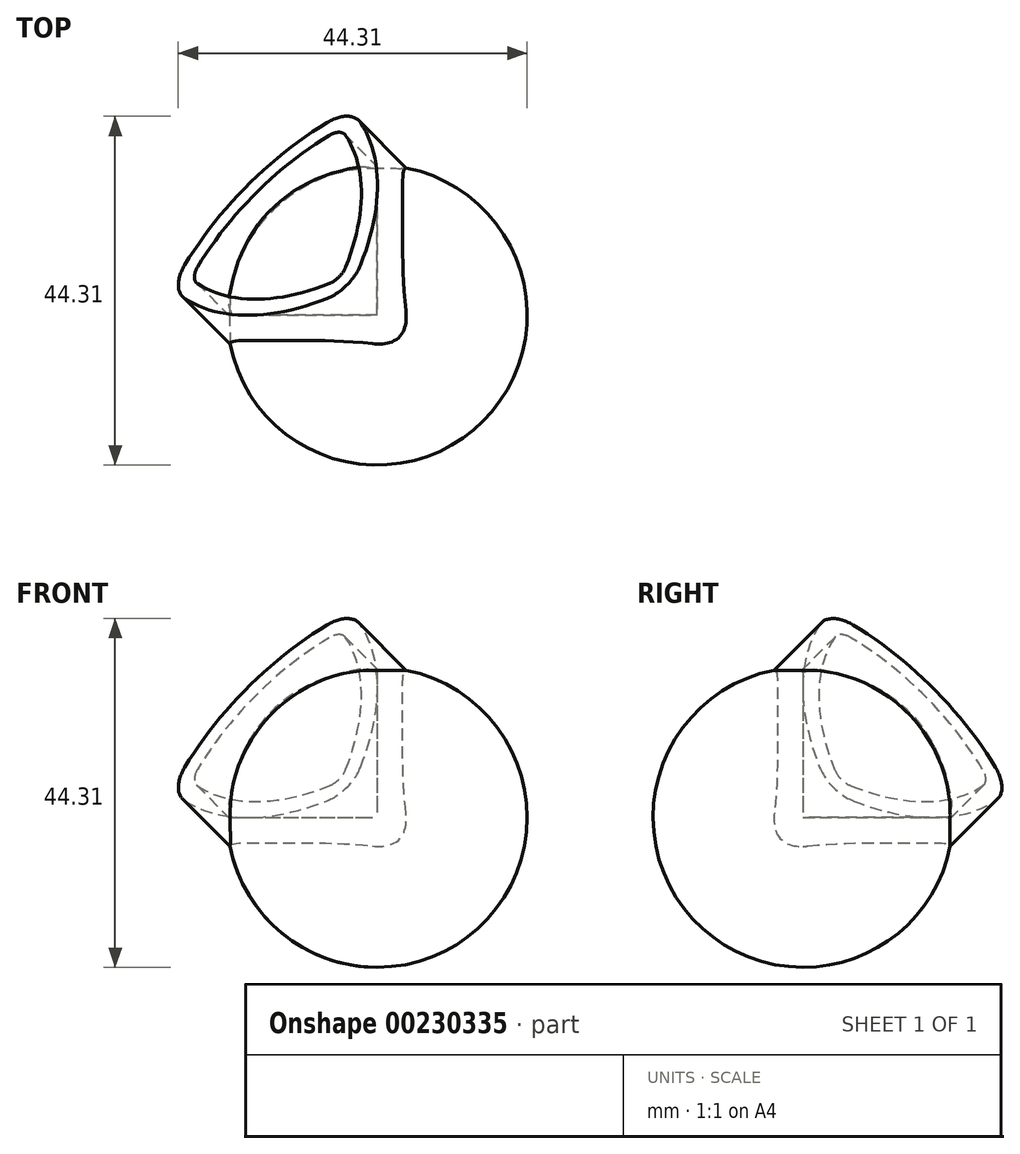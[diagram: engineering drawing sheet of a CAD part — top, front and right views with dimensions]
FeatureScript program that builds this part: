
annotation { "Feature Type Name" : "Feature", "Feature Type Description" : "" }
export const myFeature = defineFeature(function(context is Context, id is Id, definition is map)
    precondition{}
    {
        {
            var Q0;
            Q0=qCreatedBy(makeId("Front.planeOp"),FACE);
            var sketch = newSketch(context, id + "F0", { "sketchPlane" : qUnion([Q0])});
            skLineSegment(sketch, "E0", {"start": v(0, 19.05) * mm, "end": v(0, -19.05) * mm});
            skArc(sketch, "E1", {"start": v(0, 19.05) * mm, "mid": v(-19.05, 0) * mm, "end": v(0, -19.05) * mm});
            skSolve(sketch);
        }
        {
            var Q0;
            Q0=makeQuery(id+"F0.imprint","IMPRINT",FACE,{"disambiguationData":[TD([[makeQuery(id+"F0.imprint","IMPRINT",EDGE,{"derivedFrom":sQuery(id+"F0.wireOp",EDGE,"E0")}),-1.0]])]});
            var Q1;
            Q1=sQuery(id+"F0.wireOp",EDGE,"E0");
            revolve(context, id + "F1", {"entities" : qUnion([Q0]), "axis" : qUnion([Q1]), "revolveType" : RevolveType.FULL});
        }
        {
            var Q0;
            Q0=qCreatedBy(makeId("Front.planeOp"),FACE);
            var sketch = newSketch(context, id + "F2", { "sketchPlane" : qUnion([Q0])});
            skArc(sketch, "E2", {"start": v(0, 19.05) * mm, "mid": v(-13.47, 13.47) * mm, "end": v(-19.05, 0) * mm});
            skLineSegment(sketch, "E3", {"start": v(-19.05, 0) * mm, "end": v(0, 0) * mm});
            skLineSegment(sketch, "E4", {"start": v(0, 19.05) * mm, "end": v(0, 0) * mm});
            skSolve(sketch);
        }
        {
            var Q0;
            Q0=qSketchRegion(id+"F2",true);
            extrude(context, id + "F3", {"entities" : qUnion([Q0]), "operationType" : NewBodyOperationType.REMOVE, "oppositeDirection" : true, "depth" : 25 * mm});
        }
        {
            var Q0;
            Q0=makeQuery(id+"F3.boolean.opBoolean","COPY",VERTEX,{"derivedFrom":makeQuery(id+"F3.opExtrude","CAP_VERTEX",VERTEX,{"disambiguationData":[OSD([sQuery(id+"F2.wireOp",EDGE,"E2"),sQuery(id+"F2.wireOp",EDGE,"E4")])],"isStart":true})});
            var Q1;
            Q1=makeQuery(id+"F3.boolean.opBoolean","INTERSECT",VERTEX,{"derivedFrom":[makeQuery(id+"F1.opRevolve","SWEPT_FACE",FACE,{"disambiguationData":[OSD([sQuery(id+"F0.wireOp",EDGE,"E1")])]}),makeQuery(id+"F3.opExtrude","SWEPT_FACE",FACE,{"disambiguationData":[OSD([sQuery(id+"F2.wireOp",EDGE,"E3")])]}),makeQuery(id+"F3.opExtrude","SWEPT_FACE",FACE,{"disambiguationData":[OSD([sQuery(id+"F2.wireOp",EDGE,"E4")])]})]});
            var Q2;
            Q2=makeQuery(id+"F3.boolean.opBoolean","COPY",VERTEX,{"derivedFrom":makeQuery(id+"F3.opExtrude","CAP_VERTEX",VERTEX,{"disambiguationData":[OSD([sQuery(id+"F2.wireOp",EDGE,"E2"),sQuery(id+"F2.wireOp",EDGE,"E3")])],"isStart":true})});
            cPlane(context, id + "F4", {"entities" : qUnion([Q0, Q1, Q2]), "cplaneType" : CPlaneType.THREE_POINT, "offset" : 25 * mm, "width" : 150 * mm, "height" : 150 * mm});
        }
        {
            var Q0;
            Q0=qCreatedBy(id+"F4.planeOp",FACE);
            var sketch = newSketch(context, id + "F5", { "sketchPlane" : qUnion([Q0])});
            skArc(sketch, "E5", {"start": v(7.78, -13.47) * mm, "mid": v(10.97, 0) * mm, "end": v(7.78, 13.47) * mm});
            skArc(sketch, "E6", {"start": v(7.78, 13.47) * mm, "mid": v(-5.49, 9.5) * mm, "end": v(-15.55, 0) * mm});
            skArc(sketch, "E7", {"start": v(-15.55, 0) * mm, "mid": v(-5.49, -9.5) * mm, "end": v(7.78, -13.47) * mm});
            skArc(sketch, "E8.0", {"start": v(-18.5, 0) * mm, "mid": v(-6.74, -11.67) * mm, "end": v(9.25, -16.02) * mm});
            skArc(sketch, "E8.1", {"start": v(9.25, 16.02) * mm, "mid": v(-6.74, 11.67) * mm, "end": v(-18.5, 0) * mm});
            skArc(sketch, "E8.2", {"start": v(9.25, -16.02) * mm, "mid": v(13.47, 0) * mm, "end": v(9.25, 16.02) * mm});
            skSolve(sketch);
        }
        {
            var Q0;
            Q0=makeQuery(id+"F5.imprint","IMPRINT",FACE,{"disambiguationData":[TD([[makeQuery(id+"F5.imprint","IMPRINT",EDGE,{"derivedFrom":sQuery(id+"F5.wireOp",EDGE,"E5")}),-1.0]])]});
            var Q1;
            Q1=makeQuery(id+"F1.opRevolve","SWEPT_FACE",FACE,{"disambiguationData":[OSD([sQuery(id+"F0.wireOp",EDGE,"E1")])]});
            extrude(context, id + "F6", {"entities" : qUnion([Q0]), "operationType" : NewBodyOperationType.ADD, "endBoundEntityFace" : qUnion([Q1]), "depth" : 9.4 * mm, "hasSecondDirection" : true, "secondDirectionOppositeDirection" : true, "secondDirectionDepth" : 8 * mm});
        }
        {
            var Q0;
            Q0=qCreatedBy(makeId("Right.planeOp"),FACE);
            var Q1;
            Q1=qCreatedBy(makeId("Top.planeOp"),FACE);
            cPlane(context, id + "F7", {"entities" : qUnion([Q0, Q1]), "cplaneType" : CPlaneType.MID_PLANE, "offset" : 25 * mm, "flipAlignment" : true, "width" : 150 * mm, "height" : 150 * mm});
        }
        {
            var Q0;
            Q0=makeQuery(id+"F6.opExtrude","SWEPT_EDGE",EDGE,{"disambiguationData":[OSD([sQuery(id+"F5.wireOp",EDGE,"E8.1"),sQuery(id+"F5.wireOp",EDGE,"E8.2")])]});
            var Q1;
            Q1=makeQuery(id+"F6.opExtrude","SWEPT_EDGE",EDGE,{"disambiguationData":[OSD([sQuery(id+"F5.wireOp",EDGE,"E8.0"),sQuery(id+"F5.wireOp",EDGE,"E8.2")])]});
            var Q2;
            Q2=makeQuery(id+"F6.opExtrude","SWEPT_EDGE",EDGE,{"disambiguationData":[OSD([sQuery(id+"F5.wireOp",EDGE,"E8.0"),sQuery(id+"F5.wireOp",EDGE,"E8.1")])]});
            fillet(context, id + "F8", {"entities" : qUnion([Q0, Q1, Q2]), "radius" : 5 * mm, "tangentPropagation" : true, "allowEdgeOverflow" : false});
        }
        {
            var Q0;
            Q0=makeQuery(id+"F6.opExtrude","SWEPT_EDGE",EDGE,{"disambiguationData":[OSD([sQuery(id+"F5.wireOp",EDGE,"E6"),sQuery(id+"F5.wireOp",EDGE,"E7")])]});
            var Q1;
            Q1=makeQuery(id+"F6.opExtrude","SWEPT_EDGE",EDGE,{"disambiguationData":[OSD([sQuery(id+"F5.wireOp",EDGE,"E5"),sQuery(id+"F5.wireOp",EDGE,"E6")])]});
            var Q2;
            Q2=makeQuery(id+"F6.opExtrude","SWEPT_EDGE",EDGE,{"disambiguationData":[OSD([sQuery(id+"F5.wireOp",EDGE,"E5"),sQuery(id+"F5.wireOp",EDGE,"E7")])]});
            fillet(context, id + "F9", {"entities" : qUnion([Q0, Q1, Q2]), "radius" : 2.5 * mm, "tangentPropagation" : true, "allowEdgeOverflow" : false});
        }
    });
